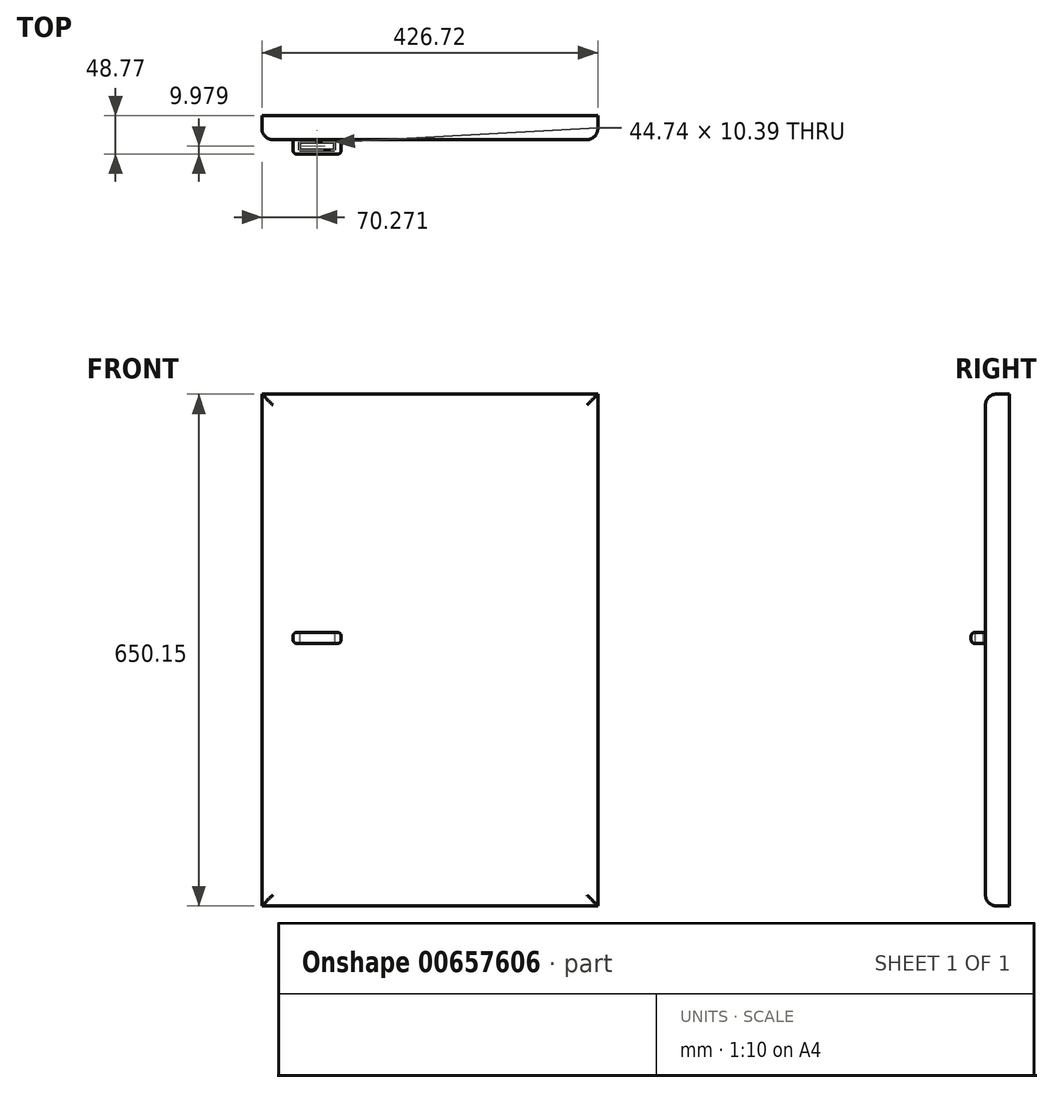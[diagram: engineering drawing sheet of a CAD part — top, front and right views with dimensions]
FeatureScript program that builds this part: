
annotation { "Feature Type Name" : "Feature", "Feature Type Description" : "" }
export const myFeature = defineFeature(function(context is Context, id is Id, definition is map)
    precondition{}
    {
        {
            var Q0;
            Q0=qCreatedBy(makeId("Front.planeOp"),FACE);
            var sketch = newSketch(context, id + "F0", { "sketchPlane" : qUnion([Q0])});
            skLineSegment(sketch, "E0.bottom", {"start": v(-439.8, 238.14) * mm, "end": v(-13.07, 238.14) * mm});
            skLineSegment(sketch, "E0.top", {"start": v(-439.8, -412.01) * mm, "end": v(-13.07, -412.01) * mm});
            skLineSegment(sketch, "E0.left", {"start": v(-439.8, 238.14) * mm, "end": v(-439.8, -412.01) * mm});
            skLineSegment(sketch, "E0.right", {"start": v(-13.07, 238.14) * mm, "end": v(-13.07, -412.01) * mm});
            skSolve(sketch);
        }
        {
            var Q0;
            Q0=makeQuery(id+"F0.imprint","IMPRINT",FACE,{"disambiguationData":[TD([[makeQuery(id+"F0.imprint","IMPRINT",EDGE,{"derivedFrom":sQuery(id+"F0.wireOp",EDGE,"E0.bottom")}),-1.0]])]});
            extrude(context, id + "F1", {"entities" : qUnion([Q0]), "depth" : 30.48 * mm, "offsetDistance" : 30.48 * mm});
        }
        {
            var Q0;
            Q0=makeQuery(id+"F1.opExtrude","CAP_EDGE",EDGE,{"disambiguationData":[OSD([sQuery(id+"F0.wireOp",EDGE,"E0.left")])],"isStart":false});
            var Q1;
            Q1=makeQuery(id+"F1.opExtrude","CAP_EDGE",EDGE,{"disambiguationData":[OSD([sQuery(id+"F0.wireOp",EDGE,"E0.bottom")])],"isStart":false});
            var Q2;
            Q2=makeQuery(id+"F1.opExtrude","CAP_EDGE",EDGE,{"disambiguationData":[OSD([sQuery(id+"F0.wireOp",EDGE,"E0.right")])],"isStart":false});
            var Q3;
            Q3=makeQuery(id+"F1.opExtrude","CAP_EDGE",EDGE,{"disambiguationData":[OSD([sQuery(id+"F0.wireOp",EDGE,"E0.top")])],"isStart":false});
            fillet(context, id + "F2", {"entities" : qUnion([Q0, Q1, Q2, Q3]), "radius" : 13.98 * mm, "tangentPropagation" : true, "allowEdgeOverflow" : false});
        }
        {
            var Q0;
            Q0=makeQuery(id+"F1.opExtrude","CAP_FACE",FACE,{"disambiguationData":[OSD([sQuery(id+"F0.wireOp",EDGE,"E0.bottom"),sQuery(id+"F0.wireOp",EDGE,"E0.top"),sQuery(id+"F0.wireOp",EDGE,"E0.left"),sQuery(id+"F0.wireOp",EDGE,"E0.right")])],"isStart":false});
            var sketch = newSketch(context, id + "F3", { "sketchPlane" : qUnion([Q0])});
            skLineSegment(sketch, "E1.bottom", {"start": v(-400.11, -64.67) * mm, "end": v(-338.99, -64.67) * mm});
            skLineSegment(sketch, "E1.top", {"start": v(-400.11, -78.55) * mm, "end": v(-338.99, -78.55) * mm});
            skLineSegment(sketch, "E1.left", {"start": v(-400.11, -64.67) * mm, "end": v(-400.11, -78.55) * mm});
            skLineSegment(sketch, "E1.right", {"start": v(-338.99, -64.67) * mm, "end": v(-338.99, -78.55) * mm});
            skSolve(sketch);
        }
        {
            var Q0;
            Q0=makeQuery(id+"F3.imprint","IMPRINT",FACE,{"disambiguationData":[TD([[makeQuery(id+"F3.imprint","IMPRINT",EDGE,{"derivedFrom":sQuery(id+"F3.wireOp",EDGE,"E1.bottom")}),-1.0]])]});
            extrude(context, id + "F4", {"entities" : qUnion([Q0]), "operationType" : NewBodyOperationType.ADD, "depth" : 18.29 * mm, "offsetDistance" : 30.48 * mm});
        }
        {
            var Q0;
            Q0=makeQuery(id+"F4.opExtrude","SWEPT_FACE",FACE,{"disambiguationData":[OSD([sQuery(id+"F3.wireOp",EDGE,"E1.top")])]});
            var sketch = newSketch(context, id + "F5", { "sketchPlane" : qUnion([Q0])});
            skLineSegment(sketch, "E2.bottom", {"start": v(-391.89, 33.6) * mm, "end": v(-347.15, 33.6) * mm});
            skLineSegment(sketch, "E2.top", {"start": v(-391.89, 43.99) * mm, "end": v(-347.15, 43.99) * mm});
            skLineSegment(sketch, "E2.left", {"start": v(-391.89, 33.6) * mm, "end": v(-391.89, 43.99) * mm});
            skLineSegment(sketch, "E2.right", {"start": v(-347.15, 33.6) * mm, "end": v(-347.15, 43.99) * mm});
            skSolve(sketch);
        }
        {
            var Q0;
            Q0=makeQuery(id+"F5.imprint","IMPRINT",FACE,{"disambiguationData":[TD([[makeQuery(id+"F5.imprint","IMPRINT",EDGE,{"derivedFrom":sQuery(id+"F5.wireOp",EDGE,"E2.bottom")}),1.0]])]});
            extrude(context, id + "F6", {"entities" : qUnion([Q0]), "operationType" : NewBodyOperationType.REMOVE, "oppositeDirection" : true, "depth" : 39 * mm, "offsetDistance" : 30.48 * mm});
        }
        {
            var Q0;
            Q0=makeQuery(id+"F4.opExtrude","CAP_EDGE",EDGE,{"disambiguationData":[OSD([sQuery(id+"F3.wireOp",EDGE,"E1.left")])],"isStart":false});
            var Q1;
            Q1=makeQuery(id+"F4.opExtrude","CAP_EDGE",EDGE,{"disambiguationData":[OSD([sQuery(id+"F3.wireOp",EDGE,"E1.bottom")])],"isStart":false});
            var Q2;
            Q2=makeQuery(id+"F4.opExtrude","CAP_EDGE",EDGE,{"disambiguationData":[OSD([sQuery(id+"F3.wireOp",EDGE,"E1.top")])],"isStart":false});
            var Q3;
            Q3=makeQuery(id+"F4.opExtrude","SWEPT_EDGE",EDGE,{"disambiguationData":[OSD([sQuery(id+"F3.wireOp",EDGE,"E1.bottom"),sQuery(id+"F3.wireOp",EDGE,"E1.right")])]});
            var Q4;
            Q4=makeQuery(id+"F4.opExtrude","CAP_EDGE",EDGE,{"disambiguationData":[OSD([sQuery(id+"F3.wireOp",EDGE,"E1.right")])],"isStart":false});
            var Q5;
            Q5=makeQuery(id+"F4.opExtrude","SWEPT_EDGE",EDGE,{"disambiguationData":[OSD([sQuery(id+"F3.wireOp",EDGE,"E1.top"),sQuery(id+"F3.wireOp",EDGE,"E1.right")])]});
            var Q6;
            Q6=makeQuery(id+"F4.opExtrude","SWEPT_EDGE",EDGE,{"disambiguationData":[OSD([sQuery(id+"F3.wireOp",EDGE,"E1.top"),sQuery(id+"F3.wireOp",EDGE,"E1.left")])]});
            var Q7;
            Q7=makeQuery(id+"F4.opExtrude","SWEPT_EDGE",EDGE,{"disambiguationData":[OSD([sQuery(id+"F3.wireOp",EDGE,"E1.bottom"),sQuery(id+"F3.wireOp",EDGE,"E1.left")])]});
            fillet(context, id + "F7", {"entities" : qUnion([Q0, Q1, Q2, Q3, Q4, Q5, Q6, Q7]), "radius" : 4.57 * mm, "tangentPropagation" : true, "allowEdgeOverflow" : false});
        }
    });
